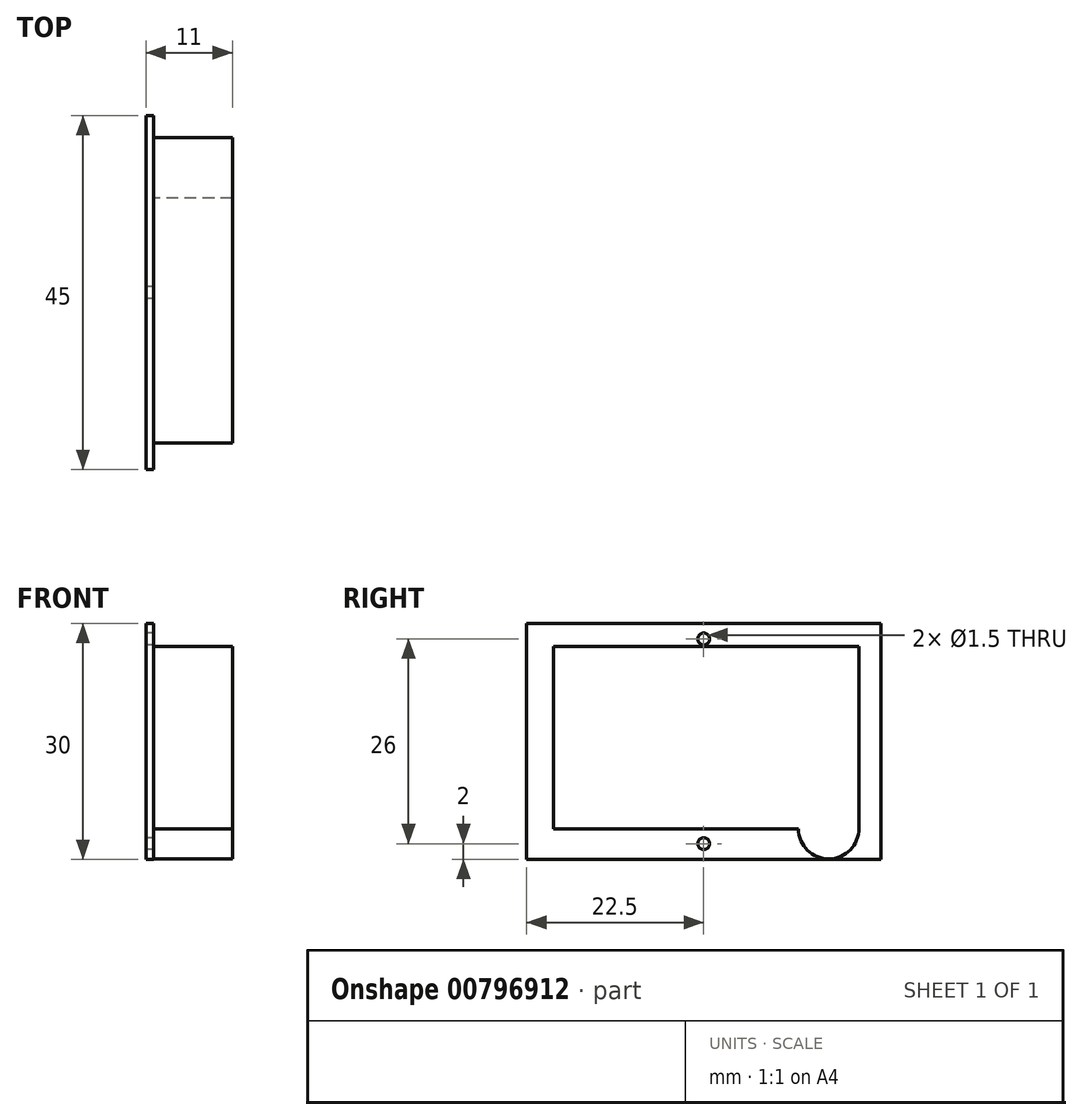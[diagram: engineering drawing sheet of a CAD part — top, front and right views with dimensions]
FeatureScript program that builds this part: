
annotation { "Feature Type Name" : "Feature", "Feature Type Description" : "" }
export const myFeature = defineFeature(function(context is Context, id is Id, definition is map)
    precondition{}
    {
        {
            var Q0;
            Q0=qCreatedBy(makeId("Right.planeOp"),FACE);
            var sketch = newSketch(context, id + "F0", { "sketchPlane" : qUnion([Q0])});
            skLineSegment(sketch, "E0.bottom", {"start": v(0, 0) * mm, "end": v(45, 0) * mm});
            skLineSegment(sketch, "E0.top", {"start": v(0, 30) * mm, "end": v(45, 30) * mm});
            skLineSegment(sketch, "E0.left", {"start": v(0, 0) * mm, "end": v(0, 30) * mm});
            skLineSegment(sketch, "E0.right", {"start": v(45, 0) * mm, "end": v(45, 30) * mm});
            skCircle(sketch, "E1", {"center": v(22.5, 28) * mm, "radius": 0.75 * mm});
            skCircle(sketch, "E2", {"center": v(22.5, 2) * mm, "radius": 0.75 * mm});
            skSolve(sketch);
        }
        {
            var Q0;
            Q0=makeQuery(id+"F0.imprint","IMPRINT",FACE,{"disambiguationData":[TD([[makeQuery(id+"F0.imprint","IMPRINT",EDGE,{"derivedFrom":sQuery(id+"F0.wireOp",EDGE,"E0.bottom")}),1.0]])]});
            extrude(context, id + "F1", {"entities" : qUnion([Q0]), "depth" : 1 * mm, "offsetDistance" : 25 * mm});
        }
        {
            var Q0;
            Q0=makeQuery(id+"F1.opExtrude","CAP_FACE",FACE,{"disambiguationData":[OSD([sQuery(id+"F0.wireOp",EDGE,"E0.bottom"),sQuery(id+"F0.wireOp",EDGE,"E0.top"),sQuery(id+"F0.wireOp",EDGE,"E0.left"),sQuery(id+"F0.wireOp",EDGE,"E0.right"),sQuery(id+"F0.wireOp",EDGE,"E1"),sQuery(id+"F0.wireOp",EDGE,"E2")])],"isStart":false});
            var sketch = newSketch(context, id + "F2", { "sketchPlane" : qUnion([Q0])});
            skLineSegment(sketch, "E3.bottom", {"start": v(3.4, 27.03) * mm, "end": v(42.22, 27.03) * mm});
            skLineSegment(sketch, "E3.top", {"start": v(3.4, 3.87) * mm, "end": v(34.53, 3.87) * mm});
            skLineSegment(sketch, "E3.left", {"start": v(3.4, 27.03) * mm, "end": v(3.4, 3.87) * mm});
            skLineSegment(sketch, "E3.right", {"start": v(42.22, 27.03) * mm, "end": v(42.22, 3.95) * mm});
            skArc(sketch, "E4", {"start": v(34.53, 3.87) * mm, "mid": v(38.41, 0.07) * mm, "end": v(42.21, 3.95) * mm});
            skLineSegment(sketch, "E5", {"start": v(42.22, 3.95) * mm, "end": v(42.21, 3.95) * mm});
            skSolve(sketch);
        }
        {
            var Q0;
            Q0=makeQuery(id+"F2.imprint","IMPRINT",FACE,{"disambiguationData":[TD([[makeQuery(id+"F2.imprint","IMPRINT",EDGE,{"derivedFrom":sQuery(id+"F2.wireOp",EDGE,"E3.bottom")}),-1.0]])]});
            extrude(context, id + "F3", {"entities" : qUnion([Q0]), "operationType" : NewBodyOperationType.ADD, "depth" : 10 * mm, "offsetDistance" : 25 * mm});
        }
    });
